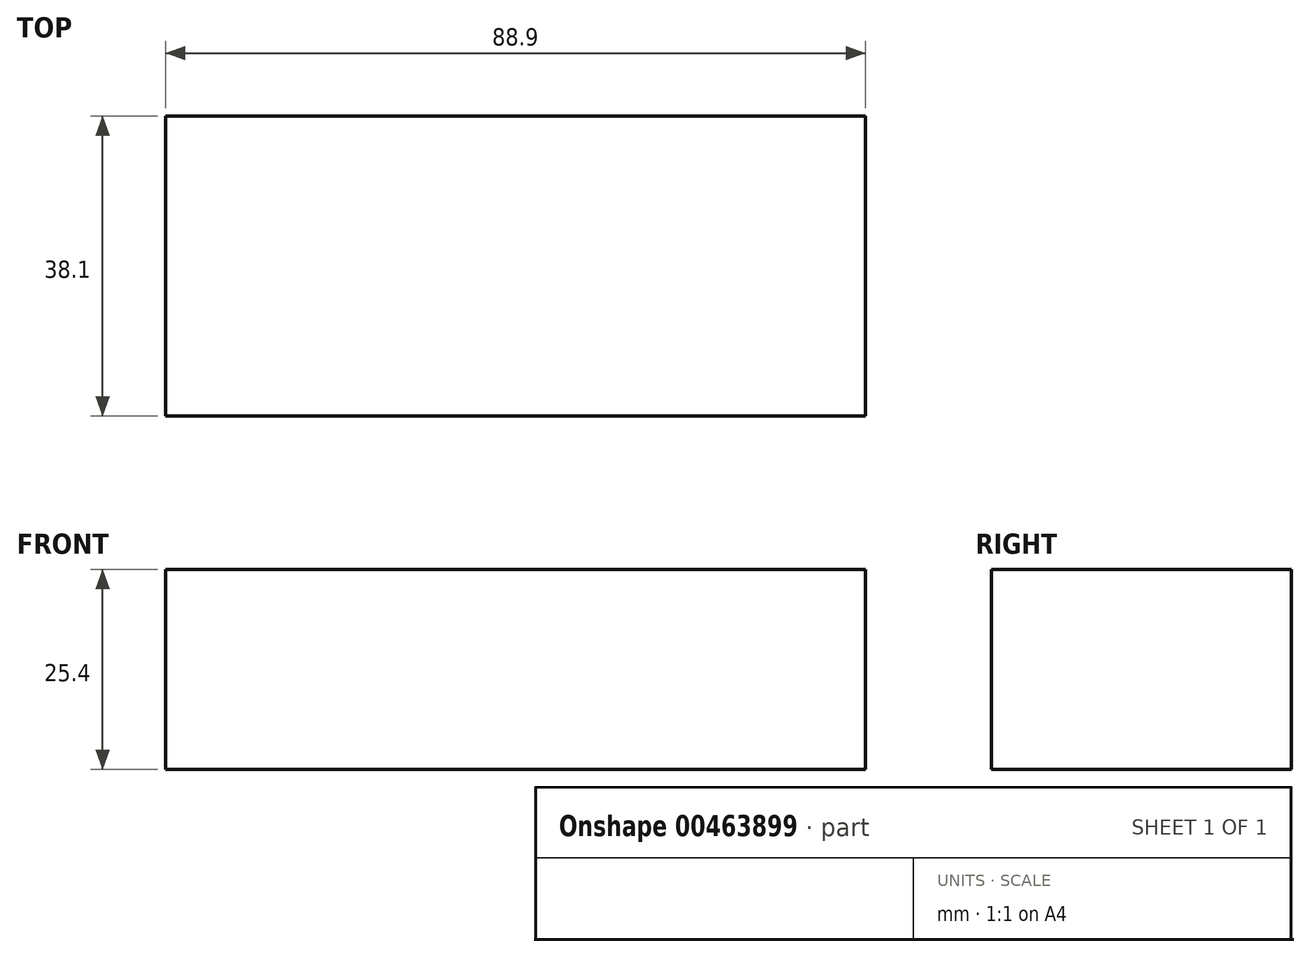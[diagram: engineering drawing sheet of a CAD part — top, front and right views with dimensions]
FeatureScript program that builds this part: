
annotation { "Feature Type Name" : "Feature", "Feature Type Description" : "" }
export const myFeature = defineFeature(function(context is Context, id is Id, definition is map)
    precondition{}
    {
        {
            var Q0;
            Q0=qCreatedBy(makeId("Top.planeOp"),FACE);
            var sketch = newSketch(context, id + "F0", { "sketchPlane" : qUnion([Q0])});
            skLineSegment(sketch, "E0.bottom", {"start": v(44.45, -19.05) * mm, "end": v(-44.45, -19.05) * mm});
            skLineSegment(sketch, "E0.top", {"start": v(44.45, 19.05) * mm, "end": v(-44.45, 19.05) * mm});
            skLineSegment(sketch, "E0.left", {"start": v(44.45, -19.05) * mm, "end": v(44.45, 19.05) * mm});
            skLineSegment(sketch, "E0.right", {"start": v(-44.45, -19.05) * mm, "end": v(-44.45, 19.05) * mm});
            skPoint(sketch, "E0.middle", {"position": v(0, 0) * mm});
            skSolve(sketch);
        }
        {
            var Q0;
            Q0=makeQuery(id+"F0.imprint","IMPRINT",FACE,{"disambiguationData":[TD([[makeQuery(id+"F0.imprint","IMPRINT",EDGE,{"derivedFrom":sQuery(id+"F0.wireOp",EDGE,"E0.bottom")}),-1.0]])]});
            extrude(context, id + "F1", {"entities" : qUnion([Q0]), "depth" : 25.4 * mm});
        }
        {
            var Q0;
            Q0=makeQuery(id+"F1.opExtrude","SWEPT_FACE",FACE,{"disambiguationData":[OSD([sQuery(id+"F0.wireOp",EDGE,"E0.bottom")])]});
            var sketch = newSketch(context, id + "F2", { "sketchPlane" : qUnion([Q0])});
            skCircle(sketch, "E1", {"center": v(28.62, 12.2) * mm, "radius": 11.12 * mm});
            skCircle(sketch, "E2.MirrorC", {"center": v(-28.62, 12.2) * mm, "radius": 11.12 * mm});
            skSolve(sketch);
        }
        {
            var Q0;
            Q0=sQuery(id+"F2.wireOp",EDGE,"E2.MirrorC");
            var Q1;
            Q1=sQuery(id+"F2.wireOp",EDGE,"E1");
            extrude(context, id + "F3", {"bodyType" : ToolBodyType.SURFACE, "surfaceEntities" : qUnion([Q0, Q1]), "oppositeDirection" : true, "depth" : 38.35 * mm});
        }
    });
